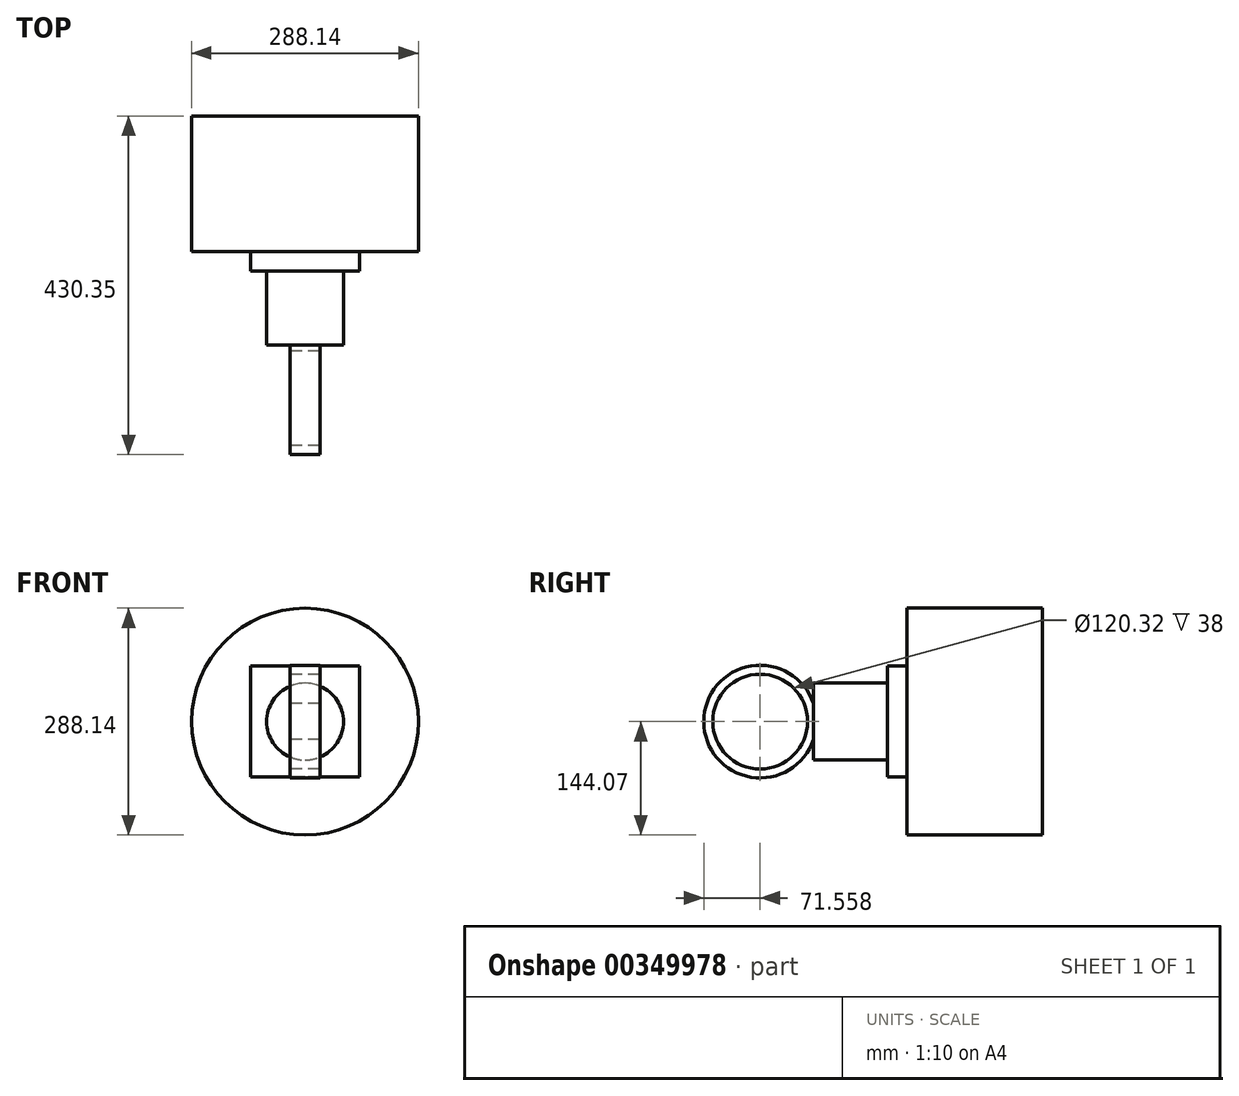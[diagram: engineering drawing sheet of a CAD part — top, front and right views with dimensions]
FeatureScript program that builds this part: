
annotation { "Feature Type Name" : "Feature", "Feature Type Description" : "" }
export const myFeature = defineFeature(function(context is Context, id is Id, definition is map)
    precondition{}
    {
        {
            var Q0;
            Q0=qCreatedBy(makeId("Front.planeOp"),FACE);
            var sketch = newSketch(context, id + "F0", { "sketchPlane" : qUnion([Q0])});
            skCircle(sketch, "E0", {"center": v(0, 0) * mm, "radius": 144.07 * mm});
            skSolve(sketch);
        }
        {
            var Q0;
            Q0 = qSketchRegion(id + "F0", true);
            extrude(context, id + "F1", {"entities" : qUnion([Q0]), "depth" : 172 * mm, "offsetDistance" : 25 * mm});
        }
        {
            var Q0;
            Q0=makeQuery(id+"F1.opExtrude","CAP_FACE",FACE,{"disambiguationData":[OSD([sQuery(id+"F0.wireOp",EDGE,"E0")])],"isStart":false});
            var sketch = newSketch(context, id + "F2", { "sketchPlane" : qUnion([Q0])});
            skLineSegment(sketch, "E1.bottom", {"start": v(68.93, -70.52) * mm, "end": v(-68.93, -70.52) * mm});
            skLineSegment(sketch, "E1.top", {"start": v(68.93, 70.52) * mm, "end": v(-68.93, 70.52) * mm});
            skLineSegment(sketch, "E1.left", {"start": v(68.93, -70.52) * mm, "end": v(68.93, 70.52) * mm});
            skLineSegment(sketch, "E1.right", {"start": v(-68.93, -70.52) * mm, "end": v(-68.93, 70.52) * mm});
            skPoint(sketch, "E1.middle", {"position": v(0, 0) * mm});
            skSolve(sketch);
        }
        {
            var Q0;
            Q0 = qSketchRegion(id + "F2", true);
            extrude(context, id + "F3", {"entities" : qUnion([Q0]), "operationType" : NewBodyOperationType.ADD, "depth" : 25 * mm, "offsetDistance" : 25 * mm});
        }
        {
            var Q0;
            Q0=makeQuery(id+"F3.opExtrude","CAP_FACE",FACE,{"disambiguationData":[OSD([sQuery(id+"F2.wireOp",EDGE,"E1.bottom"),sQuery(id+"F2.wireOp",EDGE,"E1.top"),sQuery(id+"F2.wireOp",EDGE,"E1.left"),sQuery(id+"F2.wireOp",EDGE,"E1.right")])],"isStart":false});
            var sketch = newSketch(context, id + "F4", { "sketchPlane" : qUnion([Q0])});
            skCircle(sketch, "E2", {"center": v(0, 0) * mm, "radius": 48.78 * mm});
            skSolve(sketch);
        }
        {
            var Q0;
            Q0 = qSketchRegion(id + "F4", true);
            extrude(context, id + "F5", {"entities" : qUnion([Q0]), "operationType" : NewBodyOperationType.ADD, "depth" : 94 * mm, "offsetDistance" : 25 * mm});
        }
        {
            var Q0;
            Q0=qCreatedBy(makeId("Right.planeOp"),FACE);
            var sketch = newSketch(context, id + "F6", { "sketchPlane" : qUnion([Q0])});
            skCircle(sketch, "E3", {"center": v(-358.8, 0) * mm, "radius": 71.56 * mm});
            skCircle(sketch, "E4", {"center": v(-358.8, 0) * mm, "radius": 60.16 * mm});
            skSolve(sketch);
        }
        {
            var Q0;
            Q0 = qSketchRegion(id + "F6", true);
            extrude(context, id + "F7", {"entities" : qUnion([Q0]), "operationType" : NewBodyOperationType.ADD, "endBound" : BoundingType.SYMMETRIC, "depth" : 38 * mm, "offsetDistance" : 25 * mm});
        }
    });
